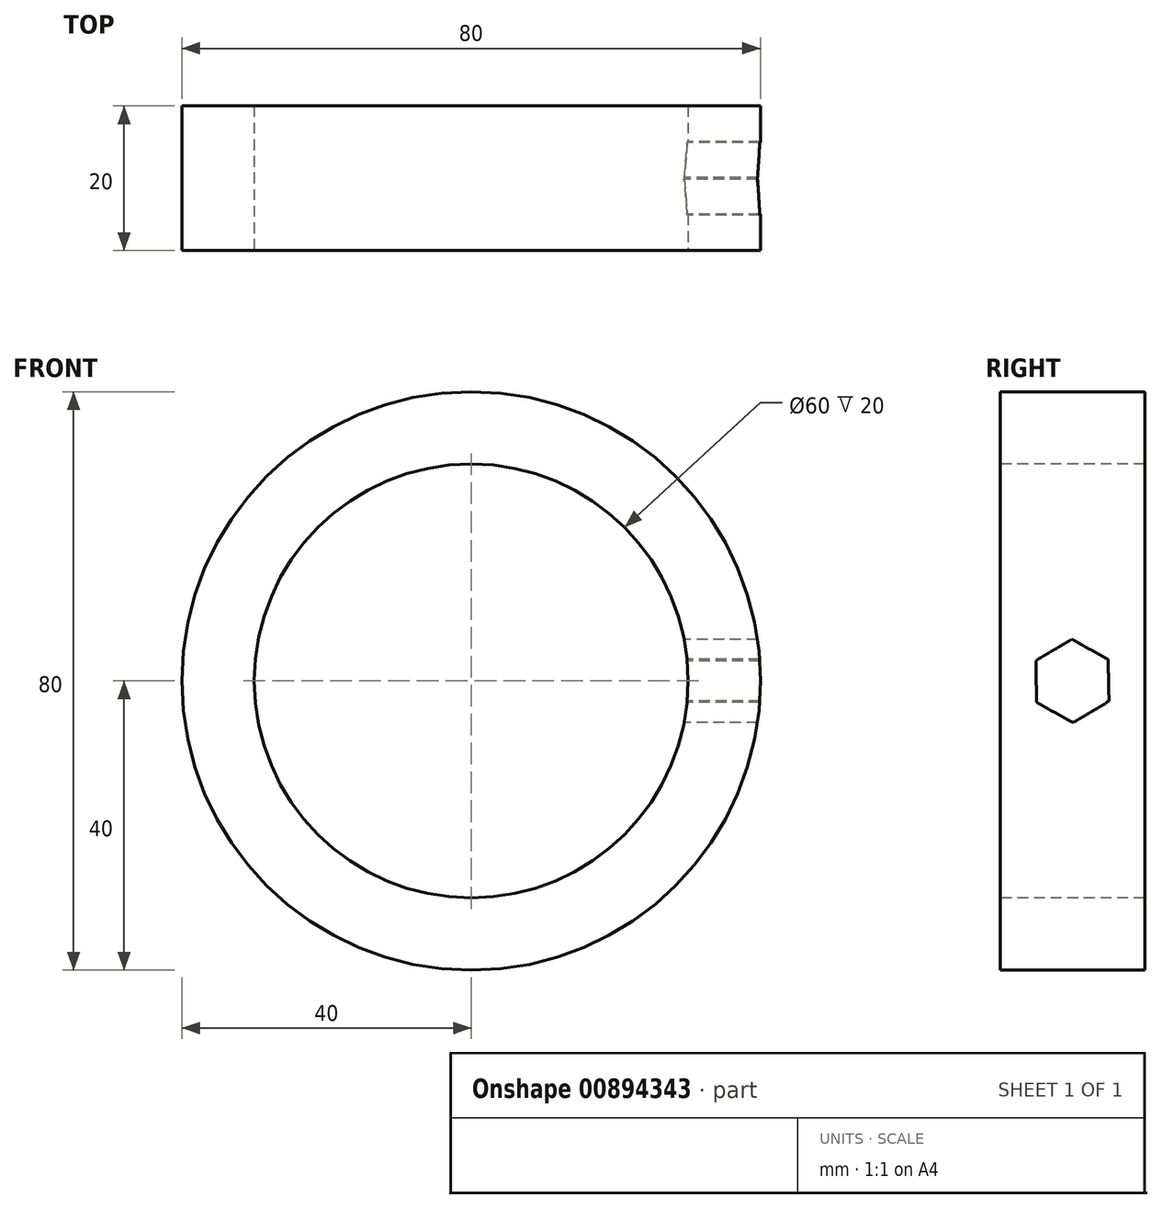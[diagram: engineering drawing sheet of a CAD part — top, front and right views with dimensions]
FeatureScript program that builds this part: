
annotation { "Feature Type Name" : "Feature", "Feature Type Description" : "" }
export const myFeature = defineFeature(function(context is Context, id is Id, definition is map)
    precondition{}
    {
        {
            var Q0;
            Q0=qCreatedBy(makeId("Front.planeOp"),FACE);
            var sketch = newSketch(context, id + "F0", { "sketchPlane" : qUnion([Q0])});
            skCircle(sketch, "E0", {"center": v(0, 0) * mm, "radius": 40 * mm});
            skSolve(sketch);
        }
        {
            var Q0;
            Q0=makeQuery(id+"F0.imprint","IMPRINT",FACE,{"disambiguationData":[TD([[makeQuery(id+"F0.imprint","IMPRINT",EDGE,{"derivedFrom":sQuery(id+"F0.wireOp",EDGE,"E0")}),1.0]])]});
            extrude(context, id + "F1", {"entities" : qUnion([Q0]), "endBound" : BoundingType.SYMMETRIC, "depth" : 20 * mm, "offsetDistance" : 25 * mm});
        }
        {
            var Q0;
            Q0=makeQuery(id+"F1.opExtrude","CAP_FACE",FACE,{"disambiguationData":[OSD([sQuery(id+"F0.wireOp",EDGE,"E0"),sQuery(id+"F0.wireOp",EDGE,"pZihG1wb-KMiZ-4XiS-56hp-MNgrY6WOYHbQ")])],"isStart":false});
            var sketch = newSketch(context, id + "F2", { "sketchPlane" : qUnion([Q0])});
            skCircle(sketch, "E1", {"center": v(0, 0) * mm, "radius": 30 * mm});
            skSolve(sketch);
        }
        {
            var Q0;
            Q0 = qSketchRegion(id + "F2", true);
            var Q1;
            Q1=makeQuery(id+"F1.opExtrude","CAP_FACE",FACE,{"disambiguationData":[OSD([sQuery(id+"F0.wireOp",EDGE,"E0")])],"isStart":true});
            extrude(context, id + "F3", {"entities" : qUnion([Q0]), "operationType" : NewBodyOperationType.REMOVE, "endBound" : BoundingType.UP_TO_SURFACE, "oppositeDirection" : true, "depth" : 47.5 * mm, "endBoundEntityFace" : qUnion([Q1]), "offsetDistance" : 25 * mm});
        }
        {
            var Q0;
            Q0=qCreatedBy(makeId("Right.planeOp"),FACE);
            var sketch = newSketch(context, id + "F4", { "sketchPlane" : qUnion([Q0])});
            skCircle(sketch, "E2.cCircle", {"center": v(0, 0) * mm, "radius": 5 * mm, "construction": true});
            skLineSegment(sketch, "E2.0", {"start": v(-0.11, 5.77) * mm, "end": v(4.94, 2.98) * mm});
            skLineSegment(sketch, "E2.1", {"start": v(4.94, 2.98) * mm, "end": v(5.05, -2.8) * mm});
            skLineSegment(sketch, "E2.2", {"start": v(5.05, -2.8) * mm, "end": v(0.11, -5.77) * mm});
            skLineSegment(sketch, "E2.3", {"start": v(0.11, -5.77) * mm, "end": v(-4.94, -2.98) * mm});
            skLineSegment(sketch, "E2.4", {"start": v(-4.94, -2.98) * mm, "end": v(-5.05, 2.8) * mm});
            skLineSegment(sketch, "E2.5", {"start": v(-5.05, 2.8) * mm, "end": v(-0.11, 5.77) * mm});
            skPoint(sketch, "E2.0.midPoint", {"position": v(2.42, 4.38) * mm});
            skSolve(sketch);
        }
        {
            var Q0;
            Q0 = qSketchRegion(id + "F4", true);
            extrude(context, id + "F5", {"entities" : qUnion([Q0]), "operationType" : NewBodyOperationType.REMOVE, "depth" : 60 * mm, "offsetDistance" : 25 * mm});
        }
    });
